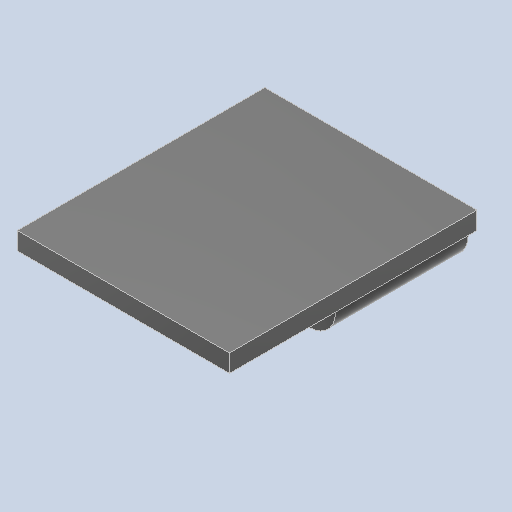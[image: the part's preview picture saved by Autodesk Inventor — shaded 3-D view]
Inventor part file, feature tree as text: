
AUTODESK INVENTOR PART (.ipt)
format: ipt  version: 2025.2 (Build 292293000, 293)  size: 110,592 bytes
history: native  units: mm
features: extrude x2, sketch x2
ambient origin geometry x8: Origin, YZ Plane, XZ Plane, XY Plane, X Axis, Y Axis, Z Axis, Center Point
bodies: Solid1 (feature_tree)
feature tree (4):
  extrude  "Extrusion1"  Depth=3.0mm
  extrude  "Extrusion2"  Depth=1.0mm
  sketch  "Sketch1"  dims[d0=3.0mm d1=9.0mm]
  sketch  "Sketch2"  dims[d2=7.5mm d3=0.0mm d4=1.0mm d5=12.0mm d6=14.0mm d7=1.0mm d8=0.0mm]
